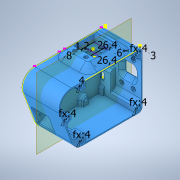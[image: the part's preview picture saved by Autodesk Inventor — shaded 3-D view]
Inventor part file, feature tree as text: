
AUTODESK INVENTOR PART (.ipt)
format: ipt  version: 2021.1 (Build 251245010, 245A)  size: 1,743,360 bytes
history: native  units: in
note: dims shown in document units (in); Inventor stores cm internally (conversion verified against a paired STEP export)
features: extrude x21, sketch x17, direct_edit x5, chamfer x5, other x4, projected_geometry x4, move_body x4, revolve x1, fillet x1, plane x1
ambient origin geometry x8: Origin, YZ Plane, XZ Plane, XY Plane, X Axis, Y Axis, Z Axis, Center Point
bodies: Solid1 (feature_tree), Body1 (feature_tree)
feature tree (63):
  sketch  "Skizze1"  dims[d0=0.1575in d1=0.1575in]
  extrude  "Extrusion2"  Depth=0.1575in
  extrude  "Extrusion1"  Depth=0.1575in
  sketch  "Skizze3"  dims[d2=0.1575in d3=0.1575in]
  extrude  "Extrusion3"  Depth=0.252in TaperAngle=0.0deg
  extrude  "Extrusion4"  Depth=0.2756in TaperAngle=0.0deg
  extrude  "Extrusion5"  Depth=0.1575in
  extrude  "Extrusion6"  Depth=0.1575in
  direct_edit  "Direktbearbeitung2"
  extrude  "Extrusion8"  Depth=0.315in
  direct_edit  "Direktbearbeitung3"
  extrude  "Extrusion10"  Depth=0.1969in TaperAngle=0.0deg
  extrude  "Extrusion11"  TaperAngle=135.0deg  [1 undecoded]
  sketch  "Skizze16"  dims[d19=45.0deg d20=0.1969in d21=0.5906in d22=0.0in d23=0.0in]
  direct_edit  "Direktbearbeitung4"
  extrude  "Extrusion19"  TaperAngle=0.0deg  [1 undecoded]
  direct_edit  "Direktbearbeitung6"
  direct_edit  "Direktbearbeitung7"
  chamfer  "Fase2"  Distance=0.0157in
  extrude  "Extrusion26"  TaperAngle=135.0deg  [1 undecoded]
  chamfer  "Fase4"  Distance=0.3937in
  sketch  "Skizze29"  dims[d32=0.3937in d33=0.2362in d34=0.0in d35=0.0in d36=0.0in d37=0.0in d38=-0.0394in d39=0.0157in d40=0.0in]
  extrude  "Extrusion30"  TaperAngle=0.0deg  [1 undecoded]
  extrude  "Extrusion35"  Depth=1.0394in
  other  "Flächenverjüngung3"
  extrude  "Extrusion36"  Depth=0.0472in
  revolve  "Umdrehung1"
  sketch  "Skizze36"  dims[d45=0.3937in d46=0.0in d69=0.0in d70=0.0in d71=-0.2756in]
  fillet  "Rundung3"  Radius=0.315in
  extrude  "Extrusion37"  Depth=0.1181in TaperAngle=0.0deg
  chamfer  "Fase5"  [1 undecoded]
  plane  "Arbeitsebene2"
  extrude  "Extrusion38"  Depth=0.0197in
  extrude  "Extrusion39"  Depth=0.0197in
  extrude  "Extrusion40"  Depth=0.0157in TaperAngle=0.0deg
  chamfer  "Fase6"  Distance=0.0197in Angle=45.0deg
  extrude  "Extrusion41"  Depth=0.0197in TaperAngle=0.0deg
  chamfer  "Fase7"  Distance=0.3346in
  extrude  "Extrusion42"  Depth=0.1181in
  extrude  "Extrusion9"  TaperAngle=45.0deg  [1 undecoded]
  projected_geometry  "Projizierte Kontur2"
  sketch  "Skizze4"  dims[d4=0.1575in d5=0.252in d6=0.0in]
  sketch  "Skizze5"  dims[d7=0.2362in d8=0.0in d9=0.2756in d10=0.0in]
  sketch  "Skizze8"  dims[d11=0.1575in d12=0.0in d13=0.1575in]
  sketch  "Skizze9"  dims[d14=0.1575in d15=0.1575in]
  sketch  "Skizze10"  dims[d16=0.252in d17=0.0in d18=0.315in]
  sketch  "Skizze26"  dims[d30=0.315in d31=135.0deg]
  sketch  "Skizze35"  dims[d41=0.315in d42=135.0deg d43=0.3937in d44=0.0in]
  sketch  "Skizze37"  dims[d72=0.3937in d73=0.0in d74=1.0394in]
  projected_geometry  "Projizierte Kontur7"
  sketch  "Skizze38"  dims[d75=1.0394in d76=0.0472in d86=0.315in]
  sketch  "Skizze39"  dims[d87=0.2362in d88=0.0in d89=0.0in d90=0.1181in d104=0.0in d105=0.0in d106=-0.0787in]
  projected_geometry  "Projizierte Kontur8"
  sketch  "Skizze40"  dims[d109=0.0197in d113=0.0197in d114=0.0787in d115=45.0deg d119=0.0197in]
  projected_geometry  "Projizierte Kontur9"
  sketch  "Skizze41"  dims[d120=0.0197in d121=0.0197in d122=0.0157in d123=0.0in d124=0.0197in d125=0.0787in d126=45.0deg d133=0.0197in d134=0.0in d144=0.3346in d145=0.0in d147=0.1181in d148=45.0deg d149=0.0197in d150=0.0in d151=0.1969in d152=90.0deg d153=0.0787in d154=0.0787in d155=0.0in d156=0.0787in d157=0.0787in d158=45.0deg d159=0.3937in d160=0.0787in d161=1.9685in d162=0.0in d163=0.1969in d164=0.1969in d165=135.0deg d166=0.0394in d167=0.0in d168=0.1575in d172=0.1811in d173=0.252in d174=0.0in d175=0.0197in d176=0.0787in d177=45.0deg d178=0.1969in d179=0.1969in d180=0.0394in d181=0.0in d182=0.0197in d183=0.0787in d184=45.0deg d185=0.0157in d186=0.0in d187=0.0197in d188=0.0344in]
  other  "Löschen2"
  other  "Löschen3"
  move_body  "Verschieben1"
  other  "Löschen4"
  move_body  "Verschieben2"
  move_body  "Verschieben4"
  move_body  "Verschieben5"
note: 6 required parameter values undecoded (feature->parameter linkage not recoverable at this tier; creation-order binding heuristic only, values carry confidence <= 0.55)
